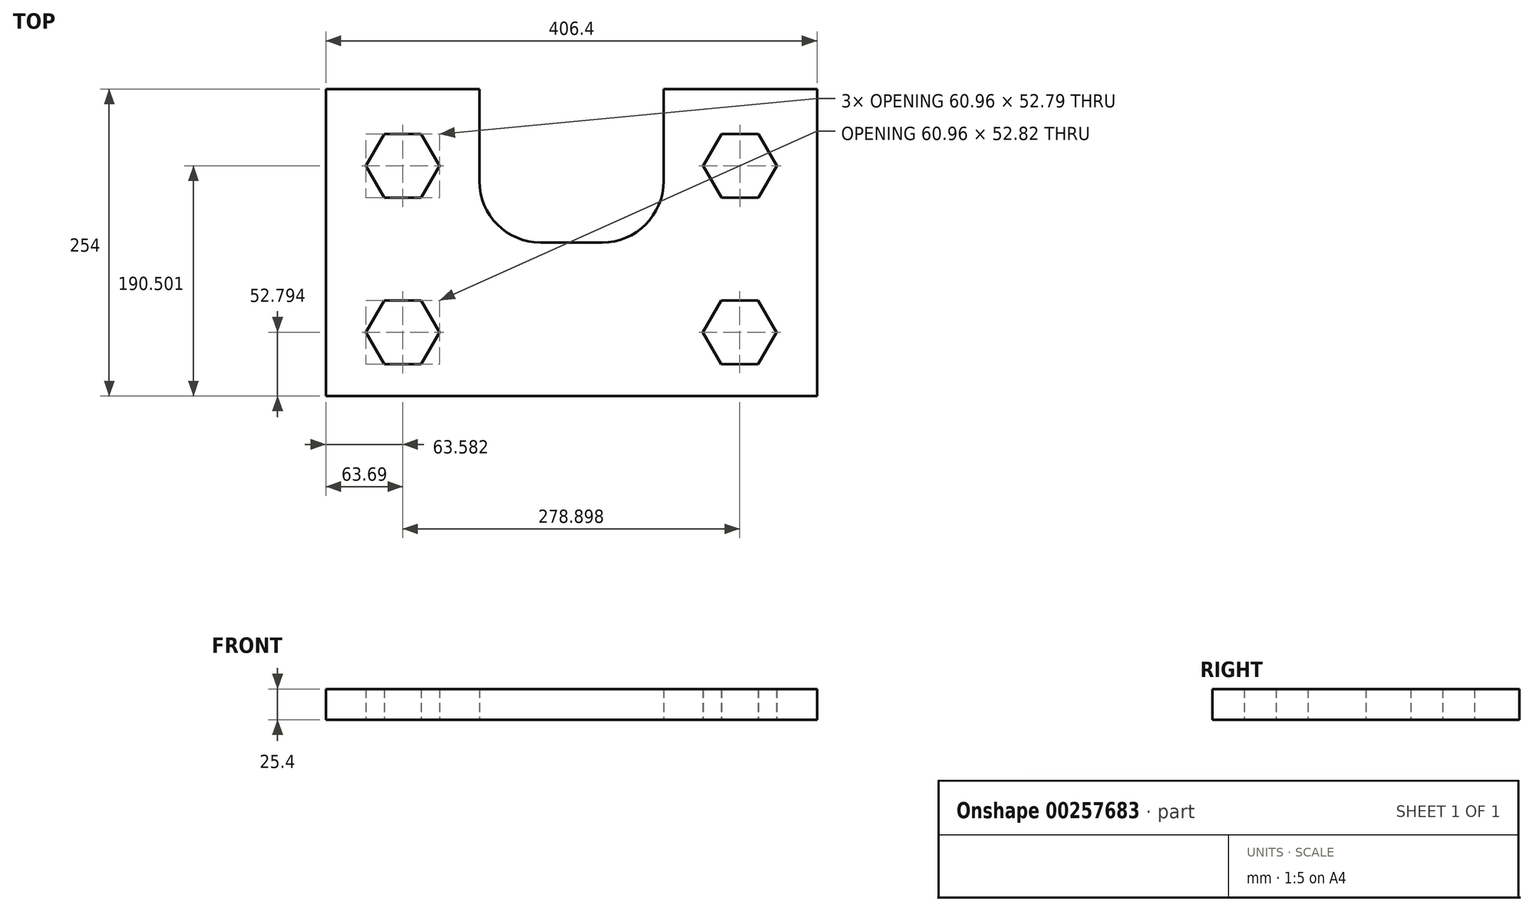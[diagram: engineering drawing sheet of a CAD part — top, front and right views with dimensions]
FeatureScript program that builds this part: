
annotation { "Feature Type Name" : "Feature", "Feature Type Description" : "" }
export const myFeature = defineFeature(function(context is Context, id is Id, definition is map)
    precondition{}
    {
        {
            var Q0;
            Q0=qCreatedBy(makeId("Top.planeOp"),FACE);
            var sketch = newSketch(context, id + "F0", { "sketchPlane" : qUnion([Q0])});
            skLineSegment(sketch, "E0", {"start": v(-135.63, -61.03) * mm, "end": v(270.77, -61.03) * mm});
            skLineSegment(sketch, "E1", {"start": v(270.77, -61.03) * mm, "end": v(270.77, 192.97) * mm});
            skLineSegment(sketch, "E2", {"start": v(270.77, 192.97) * mm, "end": v(143.77, 192.97) * mm});
            skLineSegment(sketch, "E3", {"start": v(143.77, 192.97) * mm, "end": v(143.77, 116.77) * mm});
            skLineSegment(sketch, "E4", {"start": v(92.97, 65.97) * mm, "end": v(42.17, 65.97) * mm});
            skLineSegment(sketch, "E5", {"start": v(-8.63, 116.77) * mm, "end": v(-8.63, 192.97) * mm});
            skLineSegment(sketch, "E6", {"start": v(-8.63, 192.97) * mm, "end": v(-135.63, 192.97) * mm});
            skLineSegment(sketch, "E7", {"start": v(-135.63, 192.97) * mm, "end": v(-135.63, -61.03) * mm});
            skPoint(sketch, "E8.visualSharp", {"position": v(-8.63, 65.97) * mm});
            skArc(sketch, "E8.filletArc", {"start": v(-8.63, 116.77) * mm, "mid": v(6.25, 80.85) * mm, "end": v(42.17, 65.97) * mm});
            skPoint(sketch, "E9.visualSharp", {"position": v(143.77, 65.97) * mm});
            skArc(sketch, "E9.filletArc", {"start": v(92.97, 65.97) * mm, "mid": v(128.9, 80.85) * mm, "end": v(143.77, 116.77) * mm});
            skLineSegment(sketch, "E10", {"start": v(270.77, -61.03) * mm, "end": v(270.77, -8.24) * mm});
            skLineSegment(sketch, "E11", {"start": v(237.33, -8.24) * mm, "end": v(233.25, -8.24) * mm});
            skPoint(sketch, "E12", {"position": v(270.77, -8.24) * mm});
            skLineSegment(sketch, "E13", {"start": v(270.77, -61.03) * mm, "end": v(206.85, -61.03) * mm});
            skLineSegment(sketch, "E14", {"start": v(206.85, -61.03) * mm, "end": v(270.77, -61.03) * mm});
            skLineSegment(sketch, "E15", {"start": v(270.77, 192.97) * mm, "end": v(270.77, 129.47) * mm});
            skLineSegment(sketch, "E16", {"start": v(237.56, 129.47) * mm, "end": v(233.48, 129.47) * mm});
            skLineSegment(sketch, "E17", {"start": v(-135.63, -61.03) * mm, "end": v(-71.9, -61.03) * mm});
            skCircle(sketch, "E18.cCircle", {"center": v(-71.94, -8.24) * mm, "radius": 26.4 * mm, "construction": true});
            skLineSegment(sketch, "E18.0", {"start": v(-56.68, -34.62) * mm, "end": v(-87.16, -34.64) * mm});
            skLineSegment(sketch, "E18.1", {"start": v(-87.16, -34.64) * mm, "end": v(-102.42, -8.26) * mm});
            skLineSegment(sketch, "E18.2", {"start": v(-102.42, -8.26) * mm, "end": v(-87.2, 18.15) * mm});
            skLineSegment(sketch, "E18.3", {"start": v(-87.2, 18.15) * mm, "end": v(-56.72, 18.17) * mm});
            skLineSegment(sketch, "E18.4", {"start": v(-56.72, 18.17) * mm, "end": v(-41.46, -8.21) * mm});
            skLineSegment(sketch, "E18.5", {"start": v(-41.46, -8.21) * mm, "end": v(-56.68, -34.62) * mm});
            skPoint(sketch, "E18.0.midPoint", {"position": v(-71.92, -34.63) * mm});
            skCircle(sketch, "E19.cCircle", {"center": v(206.85, -8.24) * mm, "radius": 26.4 * mm, "construction": true});
            skLineSegment(sketch, "E19.0", {"start": v(222.09, -34.63) * mm, "end": v(191.6, -34.63) * mm});
            skLineSegment(sketch, "E19.1", {"start": v(191.6, -34.63) * mm, "end": v(176.37, -8.24) * mm});
            skLineSegment(sketch, "E19.2", {"start": v(176.37, -8.24) * mm, "end": v(191.6, 18.16) * mm});
            skLineSegment(sketch, "E19.3", {"start": v(191.6, 18.16) * mm, "end": v(222.09, 18.16) * mm});
            skLineSegment(sketch, "E19.4", {"start": v(222.09, 18.16) * mm, "end": v(237.33, -8.24) * mm});
            skLineSegment(sketch, "E19.5", {"start": v(237.33, -8.24) * mm, "end": v(222.09, -34.63) * mm});
            skPoint(sketch, "E19.0.midPoint", {"position": v(206.85, -34.63) * mm});
            skCircle(sketch, "E20.cCircle", {"center": v(207.08, 129.47) * mm, "radius": 26.4 * mm, "construction": true});
            skLineSegment(sketch, "E20.0", {"start": v(222.32, 103.08) * mm, "end": v(191.84, 103.08) * mm});
            skLineSegment(sketch, "E20.1", {"start": v(191.84, 103.08) * mm, "end": v(176.6, 129.47) * mm});
            skLineSegment(sketch, "E20.2", {"start": v(176.6, 129.47) * mm, "end": v(191.84, 155.87) * mm});
            skLineSegment(sketch, "E20.3", {"start": v(191.84, 155.87) * mm, "end": v(222.32, 155.87) * mm});
            skLineSegment(sketch, "E20.4", {"start": v(222.32, 155.87) * mm, "end": v(237.56, 129.47) * mm});
            skLineSegment(sketch, "E20.5", {"start": v(237.56, 129.47) * mm, "end": v(222.32, 103.08) * mm});
            skPoint(sketch, "E20.0.midPoint", {"position": v(207.08, 103.08) * mm});
            skCircle(sketch, "E21.cCircle", {"center": v(-72.05, 129.47) * mm, "radius": 26.4 * mm, "construction": true});
            skLineSegment(sketch, "E21.0", {"start": v(-56.8, 103.08) * mm, "end": v(-87.29, 103.08) * mm});
            skLineSegment(sketch, "E21.1", {"start": v(-87.29, 103.08) * mm, "end": v(-102.53, 129.47) * mm});
            skLineSegment(sketch, "E21.2", {"start": v(-102.53, 129.47) * mm, "end": v(-87.29, 155.87) * mm});
            skLineSegment(sketch, "E21.3", {"start": v(-87.29, 155.87) * mm, "end": v(-56.8, 155.87) * mm});
            skLineSegment(sketch, "E21.4", {"start": v(-56.8, 155.87) * mm, "end": v(-41.57, 129.47) * mm});
            skLineSegment(sketch, "E21.5", {"start": v(-41.57, 129.47) * mm, "end": v(-56.8, 103.08) * mm});
            skPoint(sketch, "E21.0.midPoint", {"position": v(-72.05, 103.08) * mm});
            skLineSegment(sketch, "E22.trimOffspring", {"start": v(-98.44, 129.47) * mm, "end": v(-102.53, 129.47) * mm});
            skPoint(sketch, "E23.trimOffspring.end.orphan", {"position": v(-72.13, 192.97) * mm});
            skLineSegment(sketch, "E24.trimOffspring", {"start": v(-98.34, -8.24) * mm, "end": v(-102.4, -8.24) * mm});
            skLineSegment(sketch, "E25.trimOffspring", {"start": v(-41.47, -8.24) * mm, "end": v(-45.54, -8.24) * mm});
            skLineSegment(sketch, "E26.trimOffspring", {"start": v(180.45, -8.24) * mm, "end": v(176.37, -8.24) * mm});
            skLineSegment(sketch, "E27.trimOffspring", {"start": v(-41.57, 129.47) * mm, "end": v(-45.65, 129.47) * mm});
            skPoint(sketch, "E28.orphan", {"position": v(207.27, 192.97) * mm});
            skLineSegment(sketch, "E29.trimOffspring", {"start": v(180.69, 129.47) * mm, "end": v(176.6, 129.47) * mm});
            skSolve(sketch);
        }
        {
            var Q0;
            Q0 = qSketchRegion(id + "F0", true);
            extrude(context, id + "F1", {"entities" : qUnion([Q0]), "depth" : 25.4 * mm});
        }
    });
